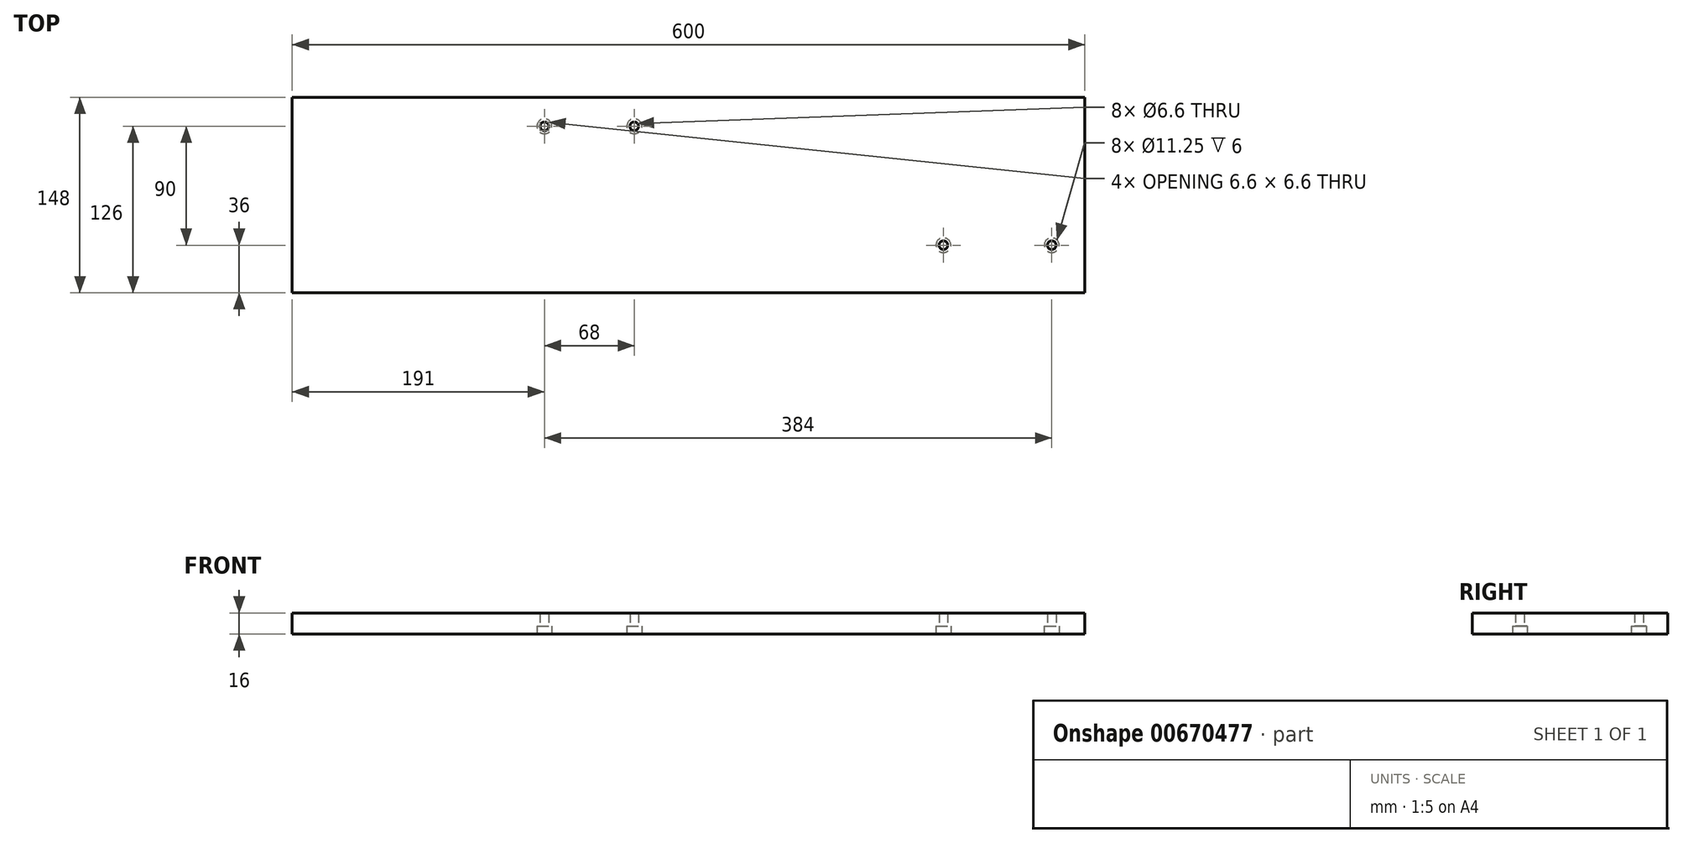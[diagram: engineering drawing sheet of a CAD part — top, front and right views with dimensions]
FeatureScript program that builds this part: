
annotation { "Feature Type Name" : "Feature", "Feature Type Description" : "" }
export const myFeature = defineFeature(function(context is Context, id is Id, definition is map)
    precondition{}
    {
        {
            var Q0;
            Q0=qCreatedBy(makeId("Top.planeOp"),FACE);
            var sketch = newSketch(context, id + "F0", { "sketchPlane" : qUnion([Q0])});
            skLineSegment(sketch, "E0.bottom", {"start": v(300, -74) * mm, "end": v(-300, -74) * mm});
            skLineSegment(sketch, "E0.top", {"start": v(300, 74) * mm, "end": v(-300, 74) * mm});
            skLineSegment(sketch, "E0.left", {"start": v(300, -74) * mm, "end": v(300, 74) * mm});
            skLineSegment(sketch, "E0.right", {"start": v(-300, -74) * mm, "end": v(-300, 74) * mm});
            skPoint(sketch, "E0.middle", {"position": v(0, 0) * mm});
            skSolve(sketch);
        }
        {
            var Q0;
            Q0=qSketchRegion(id+"F0",true);
            extrude(context, id + "F1", {"entities" : qUnion([Q0]), "depth" : 16 * mm, "offsetDistance" : 25.4 * mm});
        }
        {
            var Q0;
            Q0=makeQuery(id+"F1.opExtrude","CAP_FACE",FACE,{"disambiguationData":[OSD([sQuery(id+"F0.wireOp",EDGE,"E0.bottom"),sQuery(id+"F0.wireOp",EDGE,"E0.top"),sQuery(id+"F0.wireOp",EDGE,"E0.left"),sQuery(id+"F0.wireOp",EDGE,"E0.right")])],"isStart":false});
            var sketch = newSketch(context, id + "F2", { "sketchPlane" : qUnion([Q0])});
            skCircle(sketch, "E1", {"center": v(-109, 52) * mm, "radius": 3.3 * mm});
            skCircle(sketch, "E2", {"center": v(-41, 52) * mm, "radius": 3.3 * mm});
            skLineSegment(sketch, "E3", {"start": v(-109, 52) * mm, "end": v(-41, 52) * mm, "construction": true});
            skLineSegment(sketch, "E4", {"start": v(-75, 52) * mm, "end": v(-75, -74) * mm, "construction": true});
            skSolve(sketch);
        }
        {
            var Q0;
            Q0=makeQuery(id+"F1.opExtrude","CAP_FACE",FACE,{"disambiguationData":[OSD([sQuery(id+"F0.wireOp",EDGE,"E0.bottom"),sQuery(id+"F0.wireOp",EDGE,"E0.top"),sQuery(id+"F0.wireOp",EDGE,"E0.left"),sQuery(id+"F0.wireOp",EDGE,"E0.right")])],"isStart":false});
            var sketch = newSketch(context, id + "F3", { "sketchPlane" : qUnion([Q0])});
            skCircle(sketch, "E5", {"center": v(275, -38) * mm, "radius": 3.3 * mm});
            skCircle(sketch, "E6", {"center": v(193, -38) * mm, "radius": 3.3 * mm});
            skSolve(sketch);
        }
        {
            var Q0;
            Q0=makeQuery(id+"F1.opExtrude","CAP_FACE",FACE,{"disambiguationData":[OSD([sQuery(id+"F0.wireOp",EDGE,"E0.bottom"),sQuery(id+"F0.wireOp",EDGE,"E0.top"),sQuery(id+"F0.wireOp",EDGE,"E0.left"),sQuery(id+"F0.wireOp",EDGE,"E0.right")])],"isStart":true});
            var sketch = newSketch(context, id + "F4", { "sketchPlane" : qUnion([Q0])});
            skPoint(sketch, "E7.0", {"position": v(-109, -52) * mm});
            skPoint(sketch, "E8.0", {"position": v(-41, -52) * mm});
            skPoint(sketch, "E9.0", {"position": v(193, 38) * mm});
            skPoint(sketch, "E10.0", {"position": v(275, 38) * mm});
            skSolve(sketch);
        }
        {
            var Q0;
            Q0=sQuery(id+"F4.wireOp",VERTEX,"E7.0");
            var Q1;
            Q1=sQuery(id+"F4.wireOp",VERTEX,"E8.0");
            var Q2;
            Q2=sQuery(id+"F4.wireOp",VERTEX,"E9.0");
            var Q3;
            Q3=sQuery(id+"F4.wireOp",VERTEX,"E10.0");
            var Q4;
            Q4=makeQuery(id+"F1.opExtrude","SWEPT_BODY",BODY,{"disambiguationData":[OSD([sQuery(id+"F0.wireOp",EDGE,"E0.bottom"),sQuery(id+"F0.wireOp",EDGE,"E0.top"),sQuery(id+"F0.wireOp",EDGE,"E0.left"),sQuery(id+"F0.wireOp",EDGE,"E0.right")])]});
            hole(context, id + "F5", {"style" : HoleStyle.C_BORE, "endStyle" : HoleEndStyle.THROUGH, "standardTappedOrClearance" : lookupTablePath({ "standard" : "ISO", "fit" : "Normal", "size" : "M6", "type" : "Clearance" }), "standardBlindInLast" : lookupTablePath({ "fit" : "Standard", "standard" : "ISO", "size" : "M6", "type" : "Clearance" }), "holeDiameter" : 6.6 * mm, "cBoreDiameter" : 11.25 * mm, "cBoreDepth" : 6 * mm, "majorDiameter" : 5 * mm, "isTappedThrough" : true, "tappedDepth" : 12 * mm, "tapClearance" : 3, "startFromSketch" : true, "locations" : qUnion([Q0, Q1, Q2, Q3]), "scope" : qUnion([Q4])});
        }
    });
